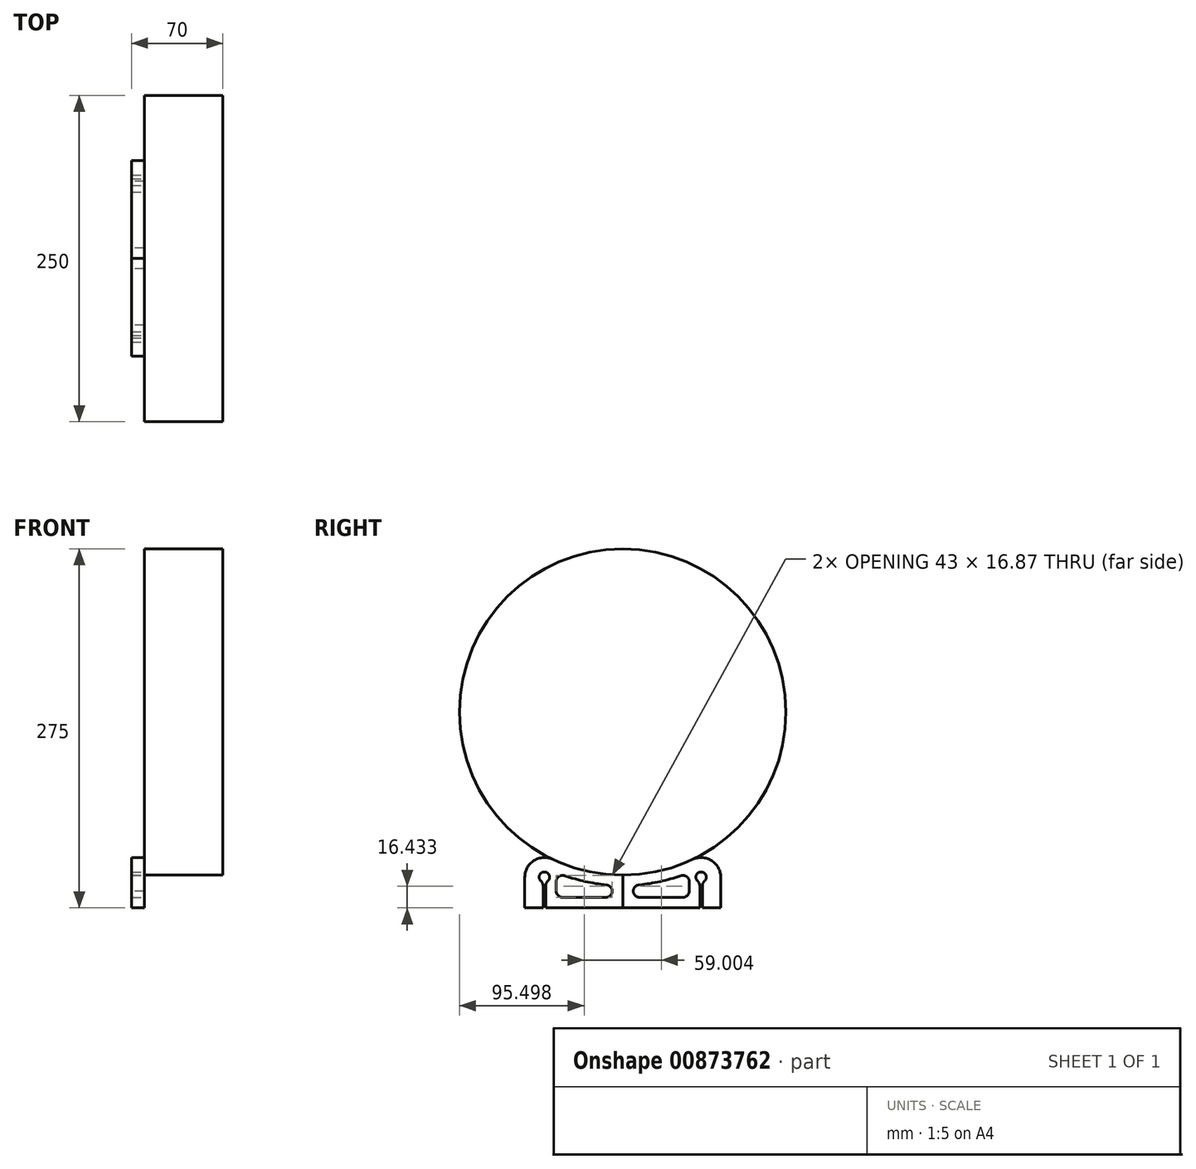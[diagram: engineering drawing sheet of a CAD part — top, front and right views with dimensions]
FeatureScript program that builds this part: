
annotation { "Feature Type Name" : "Feature", "Feature Type Description" : "" }
export const myFeature = defineFeature(function(context is Context, id is Id, definition is map)
    precondition{}
    {
        {
            var Q0;
            Q0=qCreatedBy(makeId("Right.planeOp"),FACE);
            var sketch = newSketch(context, id + "F0", { "sketchPlane" : qUnion([Q0])});
            skCircle(sketch, "E0", {"center": v(0, 0) * mm, "radius": 125 * mm});
            skSolve(sketch);
        }
        {
            var Q0;
            Q0=makeQuery(id+"F0.imprint","IMPRINT",FACE,{"disambiguationData":[TD([[makeQuery(id+"F0.imprint","IMPRINT",EDGE,{"derivedFrom":sQuery(id+"F0.wireOp",EDGE,"E0")}),1.0]])]});
            extrude(context, id + "F1", {"entities" : qUnion([Q0]), "depth" : 60 * mm, "offsetDistance" : 25 * mm});
        }
        {
            var Q0;
            Q0=makeQuery(id+"F1.opExtrude","CAP_FACE",FACE,{"disambiguationData":[OSD([sQuery(id+"F0.wireOp",EDGE,"E0")])],"isStart":true});
            var sketch = newSketch(context, id + "F2", { "sketchPlane" : qUnion([Q0])});
            skArc(sketch, "E1", {"start": v(-53.57, -112.94) * mm, "mid": v(-68.02, -113.81) * mm, "end": v(-75, -126.5) * mm});
            skPoint(sketch, "E2.endSnap0", {"position": v(0, -125) * mm});
            skArc(sketch, "E3", {"start": v(-59, -130.36) * mm, "mid": v(-60, -122.5) * mm, "end": v(-61, -130.36) * mm});
            skLineSegment(sketch, "E4", {"start": v(0, 0) * mm, "end": v(0, -125) * mm, "construction": true});
            skCircle(sketch, "E5", {"center": v(-60, -126.5) * mm, "radius": 11 * mm, "construction": true});
            skArc(sketch, "E6.0", {"start": v(-53.57, -112.94) * mm, "mid": v(-27.46, -121.95) * mm, "end": v(0, -125) * mm});
            skLineSegment(sketch, "E7", {"start": v(0, -125) * mm, "end": v(0, -150) * mm});
            skLineSegment(sketch, "E8", {"start": v(-60, -126.5) * mm, "end": v(-60, -160.88) * mm, "construction": true});
            skLineSegment(sketch, "E9.0", {"start": v(-51, -142) * mm, "end": v(-51, -130.36) * mm});
            skLineSegment(sketch, "E9.1", {"start": v(-8, -142) * mm, "end": v(-51, -142) * mm});
            skLineSegment(sketch, "E9.2", {"start": v(-8, -132.76) * mm, "end": v(-8, -142) * mm});
            skArc(sketch, "E9.3", {"start": v(-57, -120.17) * mm, "mid": v(-33.1, -128.81) * mm, "end": v(-8, -132.76) * mm});
            skLineSegment(sketch, "E10", {"start": v(-51, -130.36) * mm, "end": v(-51, -122.83) * mm});
            skLineSegment(sketch, "E11", {"start": v(-75, -150) * mm, "end": v(-75, -126.5) * mm});
            skLineSegment(sketch, "E12", {"start": v(-61, -130.36) * mm, "end": v(-61, -150) * mm});
            skLineSegment(sketch, "E13", {"start": v(-59, -130.36) * mm, "end": v(-59, -150) * mm});
            skLineSegment(sketch, "E14", {"start": v(-59, -150) * mm, "end": v(0, -150) * mm});
            skLineSegment(sketch, "E15", {"start": v(-75, -150) * mm, "end": v(-61, -150) * mm});
            skSolve(sketch);
        }
        {
            var Q0;
            Q0=makeQuery(id+"F2.imprint","IMPRINT",FACE,{"disambiguationData":[TD([[makeQuery(id+"F2.imprint","IMPRINT",EDGE,{"derivedFrom":sQuery(id+"F2.wireOp",EDGE,"E1")}),1.0]])]});
            extrude(context, id + "F3", {"entities" : qUnion([Q0]), "depth" : 10 * mm, "offsetDistance" : 25 * mm});
        }
        {
            var Q0;
            Q0=makeQuery(id+"F3.opExtrude","SWEPT_EDGE",EDGE,{"disambiguationData":[OSD([sQuery(id+"F2.wireOp",EDGE,"E9.3"),sQuery(id+"F2.wireOp",EDGE,"E10")])]});
            var Q1;
            Q1=makeQuery(id+"F3.opExtrude","SWEPT_EDGE",EDGE,{"disambiguationData":[OSD([sQuery(id+"F2.wireOp",EDGE,"E9.0"),sQuery(id+"F2.wireOp",EDGE,"E9.1")])]});
            var Q2;
            Q2=makeQuery(id+"F3.opExtrude","SWEPT_EDGE",EDGE,{"disambiguationData":[OSD([sQuery(id+"F2.wireOp",EDGE,"E9.1"),sQuery(id+"F2.wireOp",EDGE,"E9.2")])]});
            var Q3;
            Q3=makeQuery(id+"F3.opExtrude","SWEPT_EDGE",EDGE,{"disambiguationData":[OSD([sQuery(id+"F2.wireOp",EDGE,"E9.2"),sQuery(id+"F2.wireOp",EDGE,"E9.3")])]});
            var Q4;
            Q4=makeQuery(id+"F3.opExtrude","SWEPT_EDGE",EDGE,{"disambiguationData":[OSD([sQuery(id+"F2.wireOp",EDGE,"q2uUjbVi-PTXM-Ihb4-gHDy-EyNpcrHdK0Vk"),sQuery(id+"F2.wireOp",EDGE,"7sI2yNtf-AdmQ-zTAU-7F96-BCBTINKiP0KX")])]});
            var Q5;
            Q5=makeQuery(id+"F3.opExtrude","SWEPT_EDGE",EDGE,{"disambiguationData":[OSD([sQuery(id+"F2.wireOp",EDGE,"E3"),sQuery(id+"F2.wireOp",EDGE,"3d20dba5-6cc7-4f77-b706-0cb40e9d1cd50.MirrorCS")])]});
            var Q6;
            Q6=makeQuery(id+"F3.opExtrude","SWEPT_EDGE",EDGE,{"disambiguationData":[OSD([sQuery(id+"F2.wireOp",EDGE,"E1"),sQuery(id+"F2.wireOp",EDGE,"3d20dba5-6cc7-4f77-b706-0cb40e9d1cd50.MirrorCS")])]});
            var Q7;
            Q7=makeQuery(id+"F3.opExtrude","SWEPT_EDGE",EDGE,{"disambiguationData":[OSD([sQuery(id+"F2.wireOp",EDGE,"E3"),sQuery(id+"F2.wireOp",EDGE,"7sI2yNtf-AdmQ-zTAU-7F96-BCBTINKiP0KX")])]});
            fillet(context, id + "F4", {"entities" : qUnion([Q0, Q1, Q2, Q3, Q4, Q5, Q6, Q7]), "radius" : 5 * mm, "tangentPropagation" : true, "allowEdgeOverflow" : false});
        }
        {
            var Q0;
            Q0=makeQuery(id+"F3.opExtrude","SWEPT_BODY",BODY,{"disambiguationData":[OSD([sQuery(id+"F2.wireOp",EDGE,"E1"),sQuery(id+"F2.wireOp",EDGE,"E3"),sQuery(id+"F2.wireOp",EDGE,"E6.0"),sQuery(id+"F2.wireOp",EDGE,"E7"),sQuery(id+"F2.wireOp",EDGE,"bayuzoyq-AfYo-9lfw-meQl-TVhn0SphYF7g"),sQuery(id+"F2.wireOp",EDGE,"MSQg7zHl-TVNC-J0Wt-7ACe-47dQv8yDlfOq")])]});
            var Q1;
            Q1=makeQuery(id+"F3.opExtrude","SWEPT_FACE",FACE,{"disambiguationData":[OSD([sQuery(id+"F2.wireOp",EDGE,"E7")])]});
            mirror(context, id + "F5", {"operationType" : NewBodyOperationType.ADD, "entities" : qUnion([Q0]), "mirrorPlane" : qUnion([Q1])});
        }
    });
